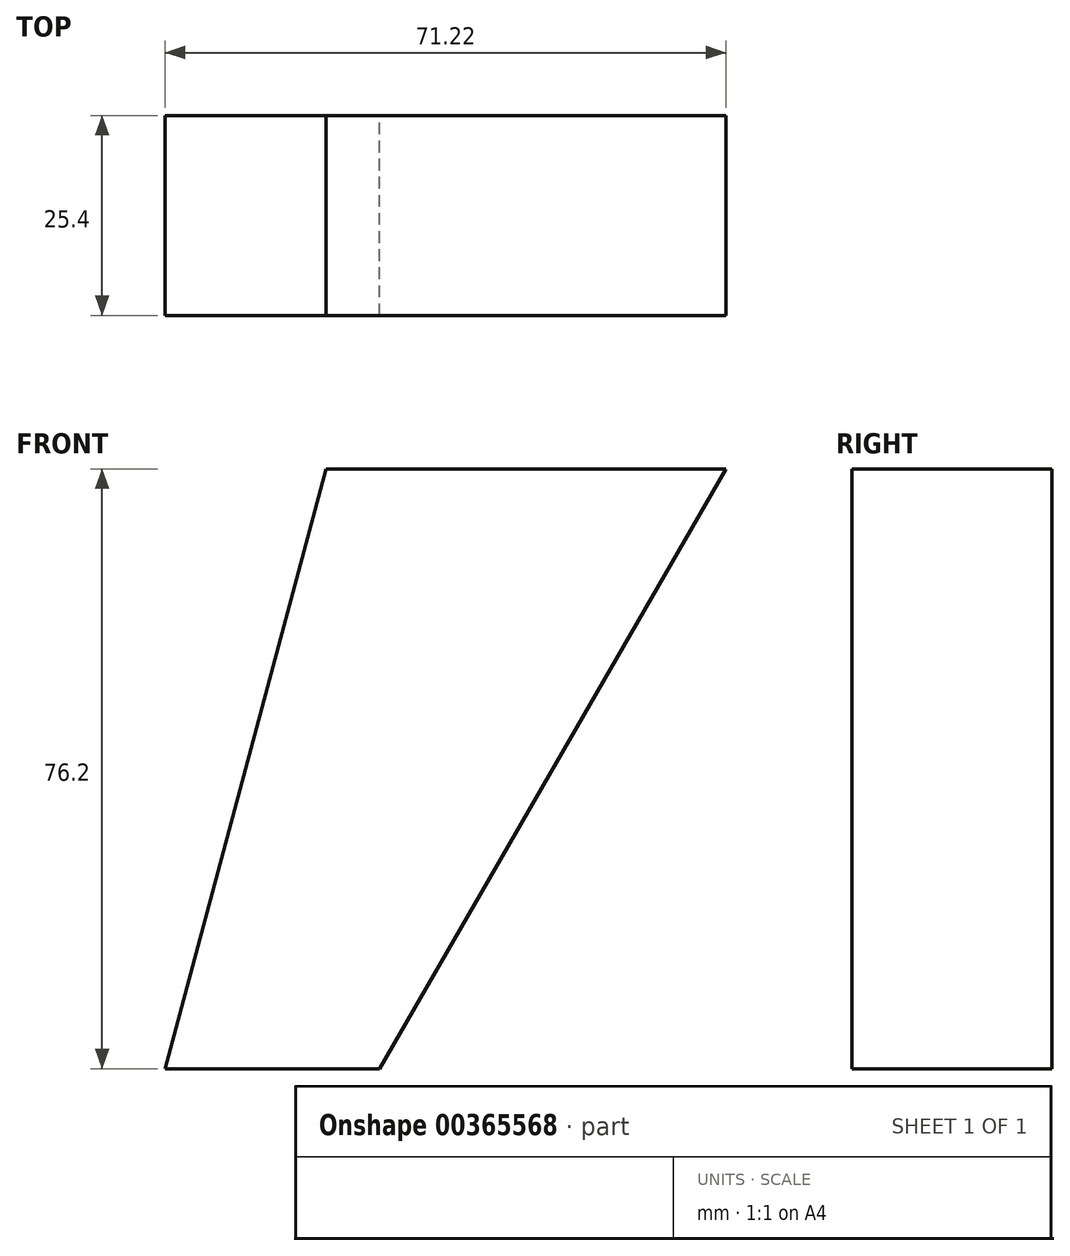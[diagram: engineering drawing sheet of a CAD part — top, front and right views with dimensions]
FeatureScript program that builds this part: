
annotation { "Feature Type Name" : "Feature", "Feature Type Description" : "" }
export const myFeature = defineFeature(function(context is Context, id is Id, definition is map)
    precondition{}
    {
        {
            var Q0;
            Q0=qCreatedBy(makeId("Front.planeOp"),FACE);
            var sketch = newSketch(context, id + "F0", { "sketchPlane" : qUnion([Q0])});
            skLineSegment(sketch, "E0", {"start": v(0, 0) * mm, "end": v(50.8, 0) * mm});
            skLineSegment(sketch, "E1", {"start": v(6.8, -76.2) * mm, "end": v(-20.42, -76.2) * mm});
            skLineSegment(sketch, "E2", {"start": v(-20.42, -76.2) * mm, "end": v(0, 0) * mm});
            skLineSegment(sketch, "E3", {"start": v(50.8, 0) * mm, "end": v(6.8, -76.2) * mm});
            skSolve(sketch);
        }
        {
            var Q0;
            Q0=makeQuery(id+"F0.imprint","IMPRINT",FACE,{"disambiguationData":[TD([[makeQuery(id+"F0.imprint","IMPRINT",EDGE,{"derivedFrom":sQuery(id+"F0.wireOp",EDGE,"E0")}),-1.0]])]});
            extrude(context, id + "F1", {"entities" : qUnion([Q0]), "depth" : 25.4 * mm});
        }
    });
